# Revit family: Sanitary_Taps-And-Mixers_Sanindusa_New-Icone-Shower-Kit
name_source: partatom
category: Plumbing Fixtures
revit_build: Autodesk Revit 2018 (Build: 20170223_1515(x64)
units: mm (PartAtom-declared; Revit-internal decimal feet)

## family parameters
Always vertical = Yes
Cut with Voids When Loaded = No
OmniClass Number = 23.45.00.00
OmniClass Title = Sanitary, Laundry, and Cleaning Equipment
Part Type = Normal
Room Calculation Point = No
Round Connector Dimension = Use Diameter
Shared = No
Work Plane-Based = No

## types (1)
- Sanitary_Taps-And-Mixers_Sanindusa_New-Icone-Shower-Kit
    AssetType = Fixed
    BodyMaterial = Brass
    CartridgeType = ceramic cartridge
    Color = Silver
    Constituents = Telescopic shower column; brass single-lever mixer, 200mm inox shower head with 1 function; ABS  hand shower with1 function; 1700mm Inox shower hose; ABS shower bracket.
    Cost = 0 $
    Description = shower kit
    Edition number = 1
    Element Type = FAUCET: A small diameter valve, with a free outlet, from which water is drawn.
    FaucetFunction = Mixed
    FaucetOperation = Other
    FaucetTopDescription = Single lever
    FaucetType = SprayMixing
    Features = Shower mixer with 2 outlets, Idealrain rainshower with fixed riser and handspray. Metal pin handles on the mixer and handsray holder. The outlet is selected using the diverter which is integral with the flow control.
    Finish = Chrome plated
    FittingCentres = 150 mm
    FlowCoefficient = Debit (3 bar): hand-shower 12 L/min - shower head 14 L/min
    FlowRateMaximum = Debit (3 bar): hand-shower 12 L/min - shower head 14 L/min
    InletConnectionType = Eccentric G 1/2" - 3/4
    Installation Instructions = https://www.tec.sanindusa.pt
    InstallationDate = 1900-12-31T23:59:59
    Manufacturer = Sanindusa
    ManufacturerName = Sanindusa
    ManufacturerURL = www.tec.sanindusa.pt
    Material = Brass
    ModelNumber = 5266701
    ModelReference = New Ícone
    Name = New ícone shower kit
    NominalHeight = 1455 mm  [stored 4.77362 ft]
    NominalLength = 280 mm  [stored 0.918635 ft]
    NominalWidth = 534 mm  [stored 1.75197 ft]
    OperatingMechanismMaterial = Brass
    Pre-defined type (IFC) = FAUCET
    Product Guid = a916a826-1132-4365-bc43-3646156db383
    Product data url = https://bimobject.com
    ProductInformation = https://www.tec.sanindusa.pt
    ProductionYear = 2018
    Size = 280x534x1455
    TestPressure = 10 bar
    Type (IFC) = IfcValveType
    URL = www.tec.sanindusa.pt
    Uniclass2015Version = Products v1.6
    ValveMechanism = UNSET
    ValveOperation = UNSET
    ValvePattern = UNSET
    Version = 1
    WarrantyDescription = https://www.tec.sanindusa.pt
    WarrantyDurationParts = 5
    WarrantyDurationUnit = year
    WarrantyStartDate = 1900-12-31T23:59:59
1900-12-31T23:59:59
    Weight = 3.70 kg
    WorkingPressure = 3 bar

note: [stored X ft] marks values corroborated as IEEE doubles in the binary element streams (Revit-internal decimal feet)

## geometry (parser evidence)
native form markers: Sweep x7
no freeform markers — native parametric forms only
